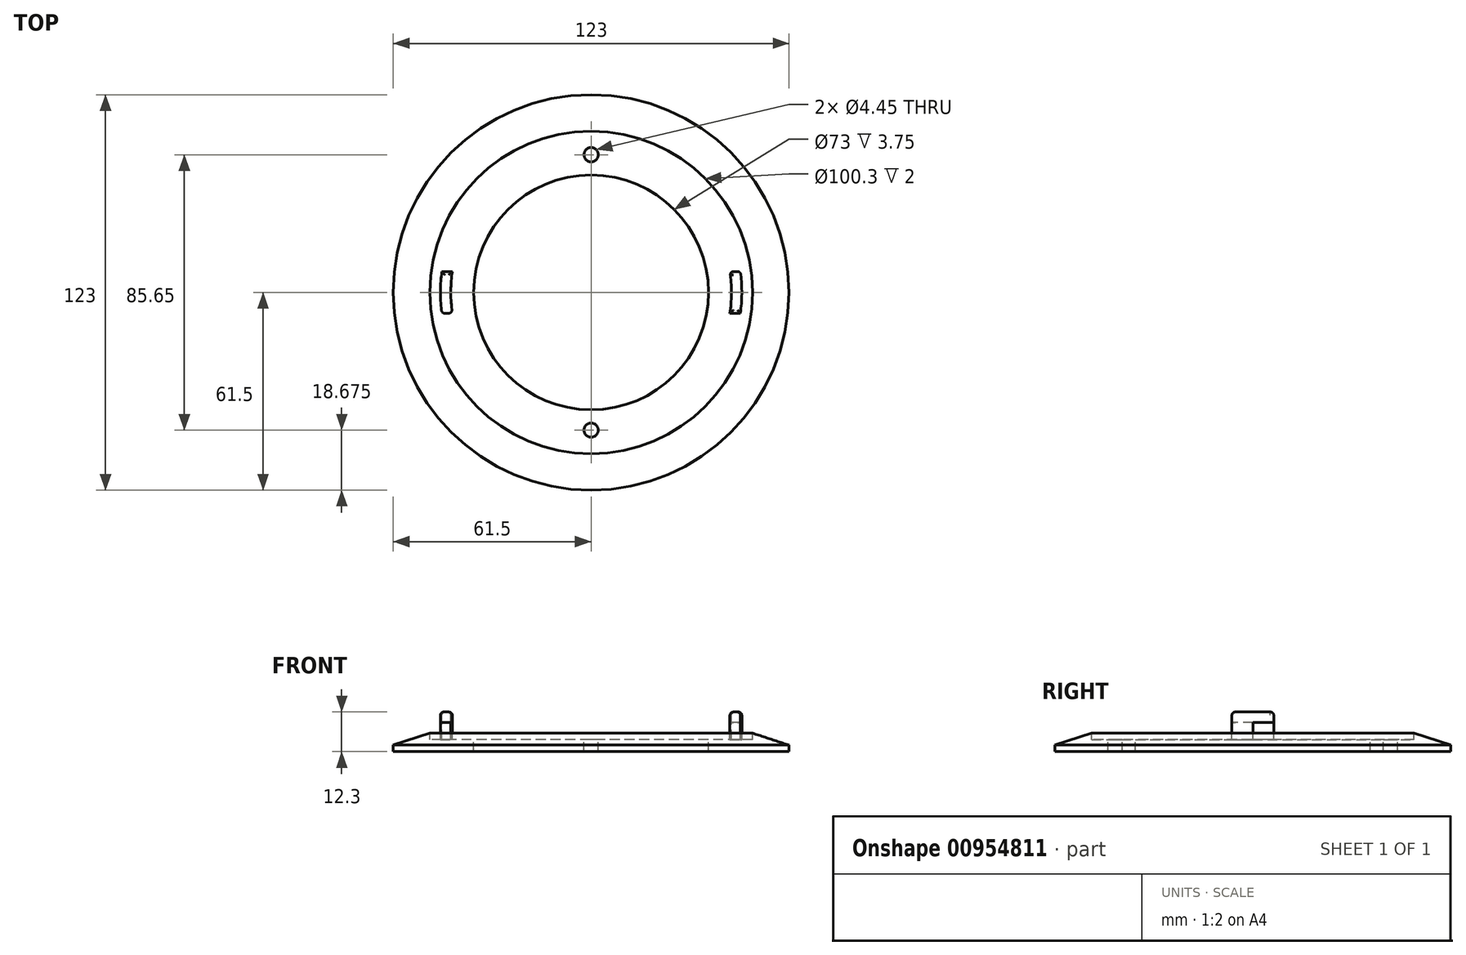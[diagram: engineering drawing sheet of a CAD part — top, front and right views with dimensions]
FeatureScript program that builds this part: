
annotation { "Feature Type Name" : "Feature", "Feature Type Description" : "" }
export const myFeature = defineFeature(function(context is Context, id is Id, definition is map)
    precondition{}
    {
        {
            var Q0;
            Q0=qCreatedBy(makeId("Top.planeOp"),FACE);
            var sketch = newSketch(context, id + "F0", { "sketchPlane" : qUnion([Q0])});
            skCircle(sketch, "E0", {"center": v(0, 0) * mm, "radius": 61.5 * mm});
            skSolve(sketch);
        }
        {
            var Q0;
            Q0=makeQuery(id+"F0.imprint","IMPRINT",FACE,{"disambiguationData":[TD([[makeQuery(id+"F0.imprint","IMPRINT",EDGE,{"derivedFrom":sQuery(id+"F0.wireOp",EDGE,"E0")}),1.0]])]});
            extrude(context, id + "F1", {"entities" : qUnion([Q0]), "depth" : 2 * mm, "offsetDistance" : 25 * mm});
        }
        {
            var Q0;
            Q0=makeQuery(id+"F1.opExtrude","CAP_FACE",FACE,{"disambiguationData":[OSD([sQuery(id+"F0.wireOp",EDGE,"E0")])],"isStart":false});
            cPlane(context, id + "F2", {"entities" : qUnion([Q0]), "cplaneType" : CPlaneType.OFFSET, "offset" : 3.75 * mm, "width" : 150 * mm, "height" : 150 * mm});
        }
        {
            var Q0;
            Q0=qCreatedBy(id+"F2.planeOp",FACE);
            var sketch = newSketch(context, id + "F3", { "sketchPlane" : qUnion([Q0])});
            skCircle(sketch, "E1", {"center": v(0, 0) * mm, "radius": 50.15 * mm});
            skSolve(sketch);
        }
        {
            var Q0;
            Q0=makeQuery(id+"F1.opExtrude","CAP_FACE",FACE,{"disambiguationData":[OSD([sQuery(id+"F0.wireOp",EDGE,"E0")])],"isStart":false});
            var sketch = newSketch(context, id + "F4", { "sketchPlane" : qUnion([Q0])});
            skCircle(sketch, "E2.0", {"center": v(0, 0) * mm, "radius": 61.5 * mm});
            skSolve(sketch);
        }
        {
            var Q1;
            Q1 = qSketchRegion(id + "F3", true);
            var Q2;
            Q2 = qSketchRegion(id + "F4", true);
            loft(context, id + "F5", {"operationType" : NewBodyOperationType.ADD, "sheetProfilesArray" : [{ "sheetProfileEntities" : qUnion([Q1]) }, { "sheetProfileEntities" : qUnion([Q2]) }]});
        }
        {
            var Q0;
            Q0=makeQuery(id+"F3.imprint","IMPRINT",FACE,{"disambiguationData":[TD([[makeQuery(id+"F3.imprint","IMPRINT",EDGE,{"derivedFrom":sQuery(id+"F3.wireOp",EDGE,"E1")}),1.0]])]});
            var sketch = newSketch(context, id + "F6", { "sketchPlane" : qUnion([Q0])});
            skCircle(sketch, "E3", {"center": v(0, 0) * mm, "radius": 36.5 * mm});
            skSolve(sketch);
        }
        {
            var Q0;
            Q0 = qSketchRegion(id + "F6", true);
            extrude(context, id + "F7", {"entities" : qUnion([Q0]), "operationType" : NewBodyOperationType.REMOVE, "endBound" : BoundingType.THROUGH_ALL, "oppositeDirection" : true, "depth" : 25 * mm, "offsetDistance" : 25 * mm});
        }
        {
            var Q0;
            Q0=makeQuery(id+"F3.imprint","IMPRINT",FACE,{"disambiguationData":[TD([[makeQuery(id+"F3.imprint","IMPRINT",EDGE,{"derivedFrom":sQuery(id+"F3.wireOp",EDGE,"E1")}),1.0]])]});
            var sketch = newSketch(context, id + "F8", { "sketchPlane" : qUnion([Q0])});
            skCircle(sketch, "E4.0", {"center": v(0, 0) * mm, "radius": 50.15 * mm});
            skCircle(sketch, "E5.0", {"center": v(0, 0) * mm, "radius": 36.5 * mm});
            skSolve(sketch);
        }
        {
            var Q0;
            Q0=makeQuery(id+"F8.imprint","IMPRINT",FACE,{"disambiguationData":[TD([[makeQuery(id+"F8.imprint","IMPRINT",EDGE,{"derivedFrom":sQuery(id+"F8.wireOp",EDGE,"E4.0")}),1.0]])]});
            extrude(context, id + "F9", {"entities" : qUnion([Q0]), "operationType" : NewBodyOperationType.REMOVE, "oppositeDirection" : true, "depth" : 2 * mm, "offsetDistance" : 25 * mm});
        }
        {
            var Q0;
            Q0=makeQuery(id+"F3.imprint","IMPRINT",FACE,{"disambiguationData":[TD([[makeQuery(id+"F3.imprint","IMPRINT",EDGE,{"derivedFrom":sQuery(id+"F3.wireOp",EDGE,"E1")}),1.0]])]});
            var sketch = newSketch(context, id + "F10", { "sketchPlane" : qUnion([Q0])});
            skCircle(sketch, "E6", {"center": v(0, 42.82) * mm, "radius": 2.23 * mm});
            skPoint(sketch, "E7.start.orphan", {"position": v(0, 36.5) * mm});
            skPoint(sketch, "E8", {"position": v(0, -36.5) * mm});
            skCircle(sketch, "E9", {"center": v(0, -42.82) * mm, "radius": 2.23 * mm});
            skSolve(sketch);
        }
        {
            var Q0;
            Q0 = qSketchRegion(id + "F10", true);
            extrude(context, id + "F11", {"entities" : qUnion([Q0]), "operationType" : NewBodyOperationType.REMOVE, "endBound" : BoundingType.THROUGH_ALL, "oppositeDirection" : true, "depth" : 25 * mm, "offsetDistance" : 25 * mm});
        }
        {
            var Q0;
            Q0=makeQuery(id+"F3.imprint","IMPRINT",FACE,{"disambiguationData":[TD([[makeQuery(id+"F3.imprint","IMPRINT",EDGE,{"derivedFrom":sQuery(id+"F3.wireOp",EDGE,"E1")}),1.0]])]});
            var sketch = newSketch(context, id + "F12", { "sketchPlane" : qUnion([Q0])});
            skArc(sketch, "E10", {"start": v(-46.4, 6.5) * mm, "mid": v(-46.85, 0) * mm, "end": v(-46.4, -6.5) * mm});
            skArc(sketch, "E11", {"start": v(-43.14, 6.5) * mm, "mid": v(-43.62, 0) * mm, "end": v(-43.14, -6.5) * mm});
            skPoint(sketch, "E12", {"position": v(43.63, 6.5) * mm});
            skPoint(sketch, "E13", {"position": v(43.63, -6.5) * mm});
            skLineSegment(sketch, "E14", {"start": v(46.4, -6.5) * mm, "end": v(43.14, -6.5) * mm});
            skLineSegment(sketch, "E15", {"start": v(46.4, 6.5) * mm, "end": v(43.14, 6.5) * mm});
            skPoint(sketch, "E16", {"position": v(-43.63, 6.5) * mm});
            skPoint(sketch, "E17", {"position": v(-43.63, -6.5) * mm});
            skLineSegment(sketch, "E18", {"start": v(-46.4, 6.5) * mm, "end": v(-43.14, 6.5) * mm});
            skLineSegment(sketch, "E19", {"start": v(-46.4, -6.5) * mm, "end": v(-43.14, -6.5) * mm});
            skArc(sketch, "E20.trimOffspring", {"start": v(46.4, -6.5) * mm, "mid": v(46.85, 0) * mm, "end": v(46.4, 6.5) * mm});
            skArc(sketch, "E21.trimOffspring", {"start": v(43.14, -6.5) * mm, "mid": v(43.63, 0) * mm, "end": v(43.14, 6.5) * mm});
            skPoint(sketch, "E22.orphan", {"position": v(-43.63, 0) * mm});
            skPoint(sketch, "E23.end.orphan", {"position": v(43.63, 0) * mm});
            skSolve(sketch);
        }
        {
            var Q0;
            Q0 = qSketchRegion(id + "F12", true);
            extrude(context, id + "F13", {"entities" : qUnion([Q0]), "operationType" : NewBodyOperationType.ADD, "endBound" : BoundingType.UP_TO_NEXT, "oppositeDirection" : true, "depth" : 25 * mm, "offsetDistance" : 25 * mm});
        }
        {
            var Q0;
            Q0=makeQuery(id+"F3.imprint","IMPRINT",FACE,{"disambiguationData":[TD([[makeQuery(id+"F3.imprint","IMPRINT",EDGE,{"derivedFrom":sQuery(id+"F3.wireOp",EDGE,"E1")}),1.0]])]});
            var sketch = newSketch(context, id + "F14", { "sketchPlane" : qUnion([Q0])});
            skLineSegment(sketch, "E24.0", {"start": v(-46.4, 6.5) * mm, "end": v(-43.14, 6.5) * mm});
            skArc(sketch, "E25.0", {"start": v(-46.4, 6.5) * mm, "mid": v(-46.85, 0) * mm, "end": v(-46.4, -6.5) * mm});
            skArc(sketch, "E26.0", {"start": v(-43.14, 6.5) * mm, "mid": v(-43.63, 0) * mm, "end": v(-43.14, -6.5) * mm});
            skLineSegment(sketch, "E27.0", {"start": v(-46.4, -6.5) * mm, "end": v(-43.14, -6.5) * mm});
            skArc(sketch, "E28.0", {"start": v(46.4, -6.5) * mm, "mid": v(46.85, 0) * mm, "end": v(46.4, 6.5) * mm});
            skArc(sketch, "E29.0", {"start": v(43.14, -6.5) * mm, "mid": v(43.63, 0) * mm, "end": v(43.14, 6.5) * mm});
            skLineSegment(sketch, "E30.0", {"start": v(46.4, -6.5) * mm, "end": v(43.14, -6.5) * mm});
            skLineSegment(sketch, "E31.0", {"start": v(46.4, 6.5) * mm, "end": v(43.14, 6.5) * mm});
            skSolve(sketch);
        }
        {
            var Q0;
            Q0 = qSketchRegion(id + "F14", true);
            extrude(context, id + "F15", {"entities" : qUnion([Q0]), "operationType" : NewBodyOperationType.ADD, "depth" : 6.55 * mm, "offsetDistance" : 25 * mm});
        }
        {
            var Q0;
            Q0=makeQuery(id+"F15.opExtrude","CAP_VERTEX",VERTEX,{"disambiguationData":[OSD([sQuery(id+"F14.wireOp",EDGE,"E26.0"),sQuery(id+"F14.wireOp",EDGE,"E27.0")])],"isStart":false});
            var Q1;
            Q1=makeQuery(id+"F15.opExtrude","CAP_VERTEX",VERTEX,{"disambiguationData":[OSD([sQuery(id+"F14.wireOp",EDGE,"E24.0"),sQuery(id+"F14.wireOp",EDGE,"E26.0")])],"isStart":false});
            var Q2;
            Q2=makeQuery(id+"F13.opExtrude","CAP_VERTEX",VERTEX,{"disambiguationData":[OSD([sQuery(id+"F12.wireOp",EDGE,"E11"),sQuery(id+"F12.wireOp",EDGE,"E19")])],"isStart":false});
            cPlane(context, id + "F16", {"entities" : qUnion([Q0, Q1, Q2]), "cplaneType" : CPlaneType.THREE_POINT, "offset" : 25 * mm, "width" : 150 * mm, "height" : 150 * mm});
        }
        {
            var Q0;
            Q0=qCreatedBy(id+"F16.planeOp",FACE);
            var sketch = newSketch(context, id + "F17", { "sketchPlane" : qUnion([Q0])});
            skLineSegment(sketch, "E32.0", {"start": v(-6.5, 3.75) * mm, "end": v(0, 3.75) * mm});
            skLineSegment(sketch, "E33.0", {"start": v(-6.5, 3.75) * mm, "end": v(-6.5, 9.05) * mm});
            skLineSegment(sketch, "E34", {"start": v(0, 3.75) * mm, "end": v(0, 9.05) * mm});
            skLineSegment(sketch, "E35", {"start": v(0, 9.05) * mm, "end": v(-6.5, 9.05) * mm});
            skPoint(sketch, "E36.orphan", {"position": v(-6.5, 12.3) * mm});
            skPoint(sketch, "E37.orphan", {"position": v(6.5, 3.75) * mm});
            skSolve(sketch);
        }
        {
            var Q0;
            Q0 = qSketchRegion(id + "F17", true);
            extrude(context, id + "F18", {"entities" : qUnion([Q0]), "operationType" : NewBodyOperationType.REMOVE, "oppositeDirection" : true, "depth" : 5 * mm, "offsetDistance" : 25 * mm});
        }
        {
            var Q0;
            Q0=makeQuery(id+"F15.opExtrude","CAP_VERTEX",VERTEX,{"disambiguationData":[OSD([sQuery(id+"F14.wireOp",EDGE,"E29.0"),sQuery(id+"F14.wireOp",EDGE,"E31.0")])],"isStart":false});
            var Q1;
            Q1=makeQuery(id+"F13.opExtrude","CAP_VERTEX",VERTEX,{"disambiguationData":[OSD([sQuery(id+"F12.wireOp",EDGE,"E15"),sQuery(id+"F12.wireOp",EDGE,"E21.trimOffspring")])],"isStart":false});
            var Q2;
            Q2=makeQuery(id+"F13.opExtrude","CAP_VERTEX",VERTEX,{"disambiguationData":[OSD([sQuery(id+"F12.wireOp",EDGE,"E14"),sQuery(id+"F12.wireOp",EDGE,"E21.trimOffspring")])],"isStart":false});
            cPlane(context, id + "F19", {"entities" : qUnion([Q0, Q1, Q2]), "cplaneType" : CPlaneType.THREE_POINT, "offset" : 25 * mm, "width" : 150 * mm, "height" : 150 * mm});
        }
        {
            var Q0;
            Q0=qCreatedBy(id+"F19.planeOp",FACE);
            var sketch = newSketch(context, id + "F20", { "sketchPlane" : qUnion([Q0])});
            skLineSegment(sketch, "E38.0", {"start": v(6.5, 3.75) * mm, "end": v(0, 3.75) * mm});
            skLineSegment(sketch, "E39.0", {"start": v(6.5, 3.75) * mm, "end": v(6.5, 9.05) * mm});
            skLineSegment(sketch, "E40", {"start": v(6.5, 9.05) * mm, "end": v(0, 9.05) * mm});
            skLineSegment(sketch, "E41", {"start": v(0, 9.05) * mm, "end": v(0, 3.75) * mm});
            skPoint(sketch, "E42.orphan", {"position": v(6.5, 12.3) * mm});
            skPoint(sketch, "E43.orphan", {"position": v(-6.5, 3.75) * mm});
            skSolve(sketch);
        }
        {
            var Q0;
            Q0=makeQuery(id+"F20.imprint","IMPRINT",FACE,{"disambiguationData":[TD([[makeQuery(id+"F20.imprint","IMPRINT",EDGE,{"derivedFrom":sQuery(id+"F20.wireOp",EDGE,"E38.0")}),-1.0]])]});
            extrude(context, id + "F21", {"entities" : qUnion([Q0]), "operationType" : NewBodyOperationType.REMOVE, "depth" : 4 * mm, "offsetDistance" : 25 * mm});
        }
        {
            var Q0;
            Q0=makeQuery(id+"F15.opExtrude","CAP_EDGE",EDGE,{"disambiguationData":[OSD([sQuery(id+"F14.wireOp",EDGE,"E31.0")])],"isStart":false});
            var Q1;
            Q1=makeQuery(id+"F15.opExtrude","CAP_EDGE",EDGE,{"disambiguationData":[OSD([sQuery(id+"F14.wireOp",EDGE,"E27.0")])],"isStart":false});
            var Q2;
            Q2=makeQuery(id+"F15.opExtrude","CAP_EDGE",EDGE,{"disambiguationData":[OSD([sQuery(id+"F14.wireOp",EDGE,"E25.0")])],"isStart":false});
            var Q3;
            Q3=makeQuery(id+"F15.opExtrude","CAP_EDGE",EDGE,{"disambiguationData":[OSD([sQuery(id+"F14.wireOp",EDGE,"E26.0")])],"isStart":false});
            var Q4;
            Q4=makeQuery(id+"F15.opExtrude","CAP_EDGE",EDGE,{"disambiguationData":[OSD([sQuery(id+"F14.wireOp",EDGE,"E29.0")])],"isStart":false});
            var Q5;
            Q5=makeQuery(id+"F15.opExtrude","CAP_EDGE",EDGE,{"disambiguationData":[OSD([sQuery(id+"F14.wireOp",EDGE,"E28.0")])],"isStart":false});
            var Q6;
            Q6=makeQuery(id+"F15.boolean.opBoolean","MERGE",EDGE,{"derivedFrom":[makeQuery(id+"F13.opExtrude","SWEPT_EDGE",EDGE,{"disambiguationData":[OSD([sQuery(id+"F12.wireOp",EDGE,"E15"),sQuery(id+"F12.wireOp",EDGE,"E21.trimOffspring")])]}),makeQuery(id+"F15.opExtrude","SWEPT_EDGE",EDGE,{"disambiguationData":[OSD([sQuery(id+"F14.wireOp",EDGE,"E29.0"),sQuery(id+"F14.wireOp",EDGE,"E31.0")])]})]});
            var Q7;
            Q7=makeQuery(id+"F15.boolean.opBoolean","MERGE",EDGE,{"derivedFrom":[makeQuery(id+"F13.opExtrude","SWEPT_EDGE",EDGE,{"disambiguationData":[OSD([sQuery(id+"F12.wireOp",EDGE,"E10"),sQuery(id+"F12.wireOp",EDGE,"E19")])]}),makeQuery(id+"F15.opExtrude","SWEPT_EDGE",EDGE,{"disambiguationData":[OSD([sQuery(id+"F14.wireOp",EDGE,"E25.0"),sQuery(id+"F14.wireOp",EDGE,"E27.0")])]})]});
            var Q8;
            Q8=makeQuery(id+"F15.boolean.opBoolean","MERGE",EDGE,{"derivedFrom":[makeQuery(id+"F13.opExtrude","SWEPT_EDGE",EDGE,{"disambiguationData":[OSD([sQuery(id+"F12.wireOp",EDGE,"E11"),sQuery(id+"F12.wireOp",EDGE,"E19")])]}),makeQuery(id+"F15.opExtrude","SWEPT_EDGE",EDGE,{"disambiguationData":[OSD([sQuery(id+"F14.wireOp",EDGE,"E26.0"),sQuery(id+"F14.wireOp",EDGE,"E27.0")])]})]});
            var Q9;
            Q9=makeQuery(id+"F15.boolean.opBoolean","MERGE",EDGE,{"derivedFrom":[makeQuery(id+"F13.opExtrude","SWEPT_EDGE",EDGE,{"disambiguationData":[OSD([sQuery(id+"F12.wireOp",EDGE,"E15"),sQuery(id+"F12.wireOp",EDGE,"E20.trimOffspring")])]}),makeQuery(id+"F15.opExtrude","SWEPT_EDGE",EDGE,{"disambiguationData":[OSD([sQuery(id+"F14.wireOp",EDGE,"E28.0"),sQuery(id+"F14.wireOp",EDGE,"E31.0")])]})]});
            var Q10;
            Q10=makeQuery(id+"F15.opExtrude","CAP_EDGE",EDGE,{"disambiguationData":[OSD([sQuery(id+"F14.wireOp",EDGE,"E24.0")])],"isStart":false});
            var Q11;
            Q11=makeQuery(id+"F15.opExtrude","CAP_EDGE",EDGE,{"disambiguationData":[OSD([sQuery(id+"F14.wireOp",EDGE,"E30.0")])],"isStart":false});
            fillet(context, id + "F22", {"entities" : qUnion([Q0, Q1, Q2, Q3, Q4, Q5, Q6, Q7, Q8, Q9, Q10, Q11]), "radius" : 1 * mm, "tangentPropagation" : true, "allowEdgeOverflow" : false});
        }
    });
